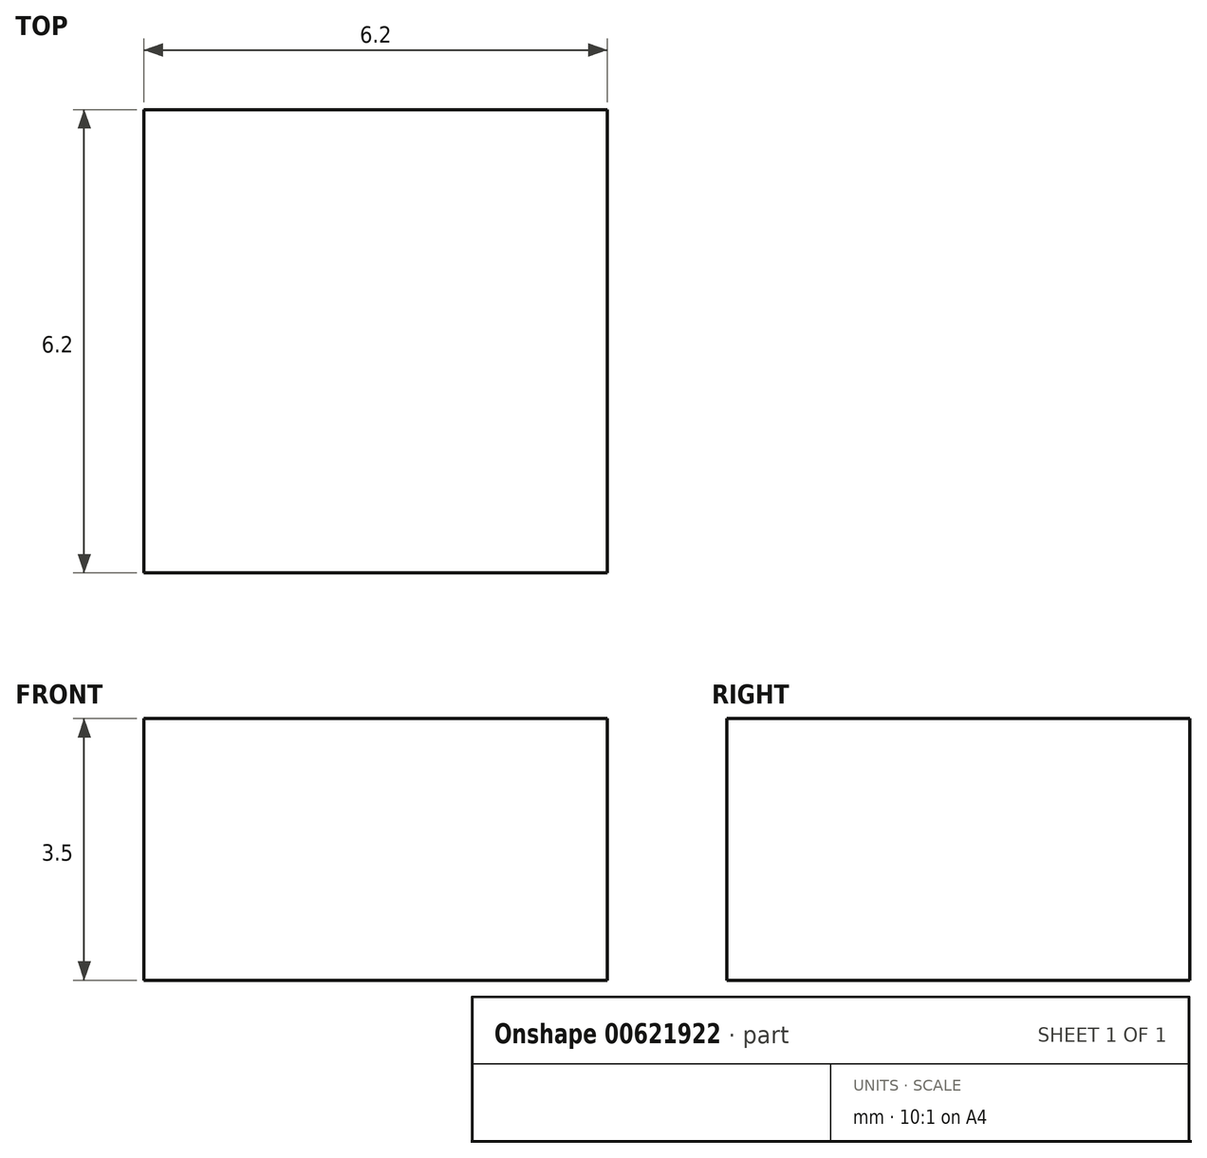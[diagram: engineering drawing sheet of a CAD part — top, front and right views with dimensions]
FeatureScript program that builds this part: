
annotation { "Feature Type Name" : "Feature", "Feature Type Description" : "" }
export const myFeature = defineFeature(function(context is Context, id is Id, definition is map)
    precondition{}
    {
        {
            var Q0;
            Q0=qCreatedBy(makeId("Top.planeOp"),FACE);
            var sketch = newSketch(context, id + "F0", { "sketchPlane" : qUnion([Q0])});
            skLineSegment(sketch, "E0.bottom", {"start": v(-3.1, 3.1) * mm, "end": v(3.1, 3.1) * mm});
            skLineSegment(sketch, "E0.top", {"start": v(-3.1, -3.1) * mm, "end": v(3.1, -3.1) * mm});
            skLineSegment(sketch, "E0.left", {"start": v(-3.1, 3.1) * mm, "end": v(-3.1, -3.1) * mm});
            skLineSegment(sketch, "E0.right", {"start": v(3.1, 3.1) * mm, "end": v(3.1, -3.1) * mm});
            skLineSegment(sketch, "E1", {"start": v(-3.1, 3.1) * mm, "end": v(3.1, -3.1) * mm});
            skSolve(sketch);
        }
        {
            var Q0;
            Q0=makeQuery(id+"F0.imprint","IMPRINT",FACE,{"disambiguationData":[TD([[makeQuery(id+"F0.imprint","IMPRINT",EDGE,{"derivedFrom":sQuery(id+"F0.wireOp",EDGE,"E0.bottom")}),-1.0]])]});
            var Q1;
            Q1=makeQuery(id+"F0.imprint","IMPRINT",FACE,{"disambiguationData":[TD([[makeQuery(id+"F0.imprint","IMPRINT",EDGE,{"derivedFrom":sQuery(id+"F0.wireOp",EDGE,"E0.top")}),1.0]])]});
            extrude(context, id + "F1", {"entities" : qUnion([Q0, Q1]), "depth" : 3.5 * mm, "offsetDistance" : 25 * mm});
        }
    });
